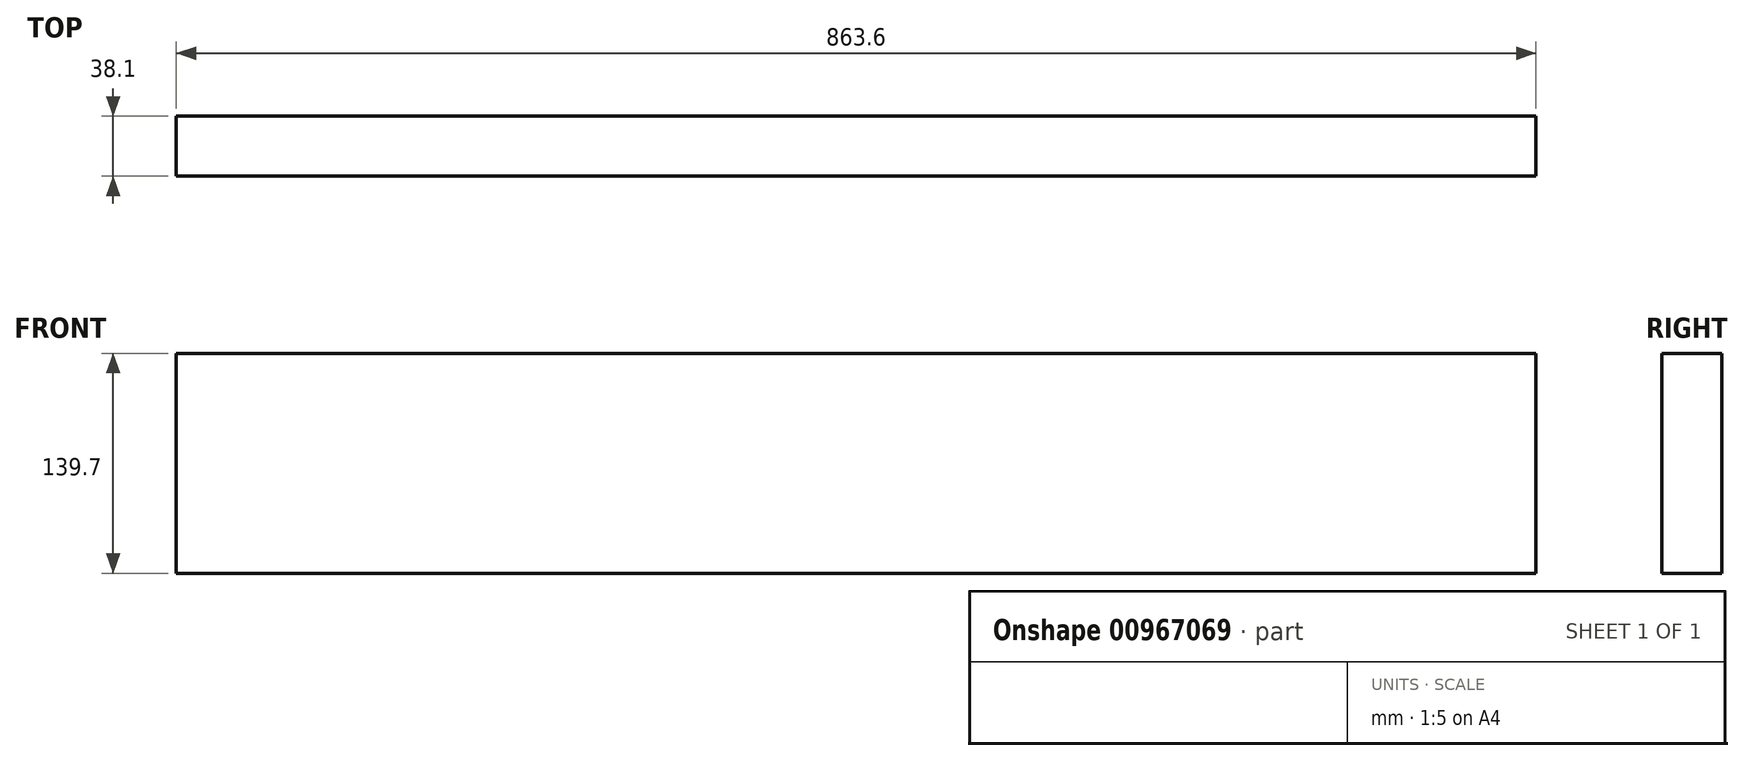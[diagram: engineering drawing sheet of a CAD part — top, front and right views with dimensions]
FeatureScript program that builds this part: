
annotation { "Feature Type Name" : "Feature", "Feature Type Description" : "" }
export const myFeature = defineFeature(function(context is Context, id is Id, definition is map)
    precondition{}
    {
        {
            var Q0;
            Q0=qCreatedBy(makeId("Right.planeOp"),FACE);
            var sketch = newSketch(context, id + "F0", { "sketchPlane" : qUnion([Q0])});
            skLineSegment(sketch, "E0.bottom", {"start": v(0, 0) * mm, "end": v(38.1, 0) * mm});
            skLineSegment(sketch, "E0.top", {"start": v(0, 139.7) * mm, "end": v(38.1, 139.7) * mm});
            skLineSegment(sketch, "E0.left", {"start": v(0, 0) * mm, "end": v(0, 139.7) * mm});
            skLineSegment(sketch, "E0.right", {"start": v(38.1, 0) * mm, "end": v(38.1, 139.7) * mm});
            skSolve(sketch);
        }
        {
            var Q0;
            Q0=qSketchRegion(id+"F0",true);
            extrude(context, id + "F1", {"entities" : qUnion([Q0]), "oppositeDirection" : true, "depth" : 863.6 * mm, "offsetDistance" : 25.4 * mm});
        }
    });
